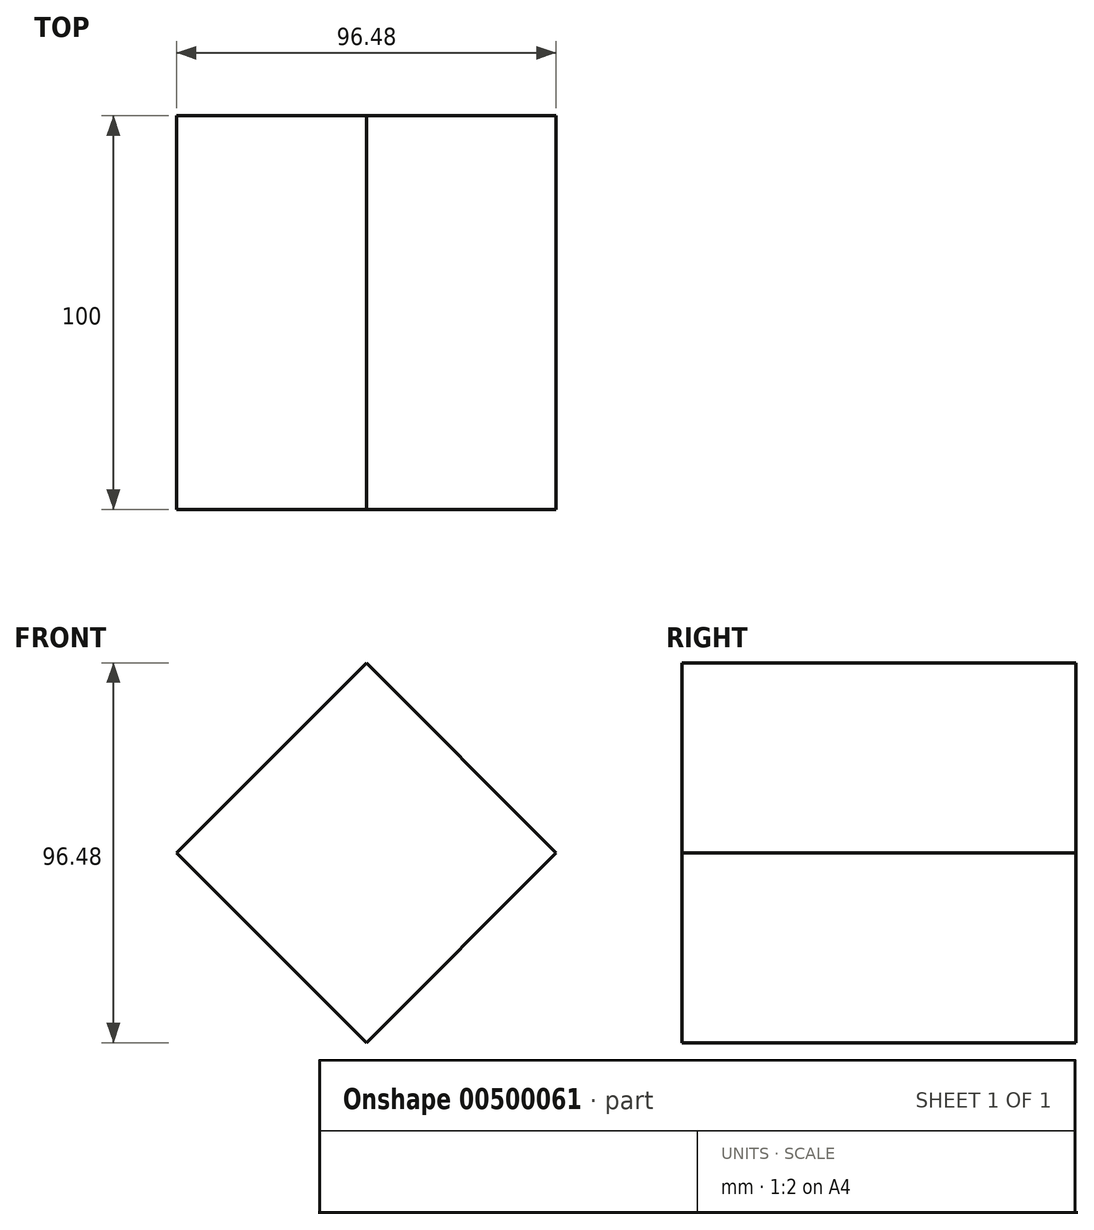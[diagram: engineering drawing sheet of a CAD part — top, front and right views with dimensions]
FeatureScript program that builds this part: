
annotation { "Feature Type Name" : "Feature", "Feature Type Description" : "" }
export const myFeature = defineFeature(function(context is Context, id is Id, definition is map)
    precondition{}
    {
        {
            var Q0;
            Q0=qCreatedBy(makeId("Front.planeOp"),FACE);
            var sketch = newSketch(context, id + "F0", { "sketchPlane" : qUnion([Q0])});
            skCircle(sketch, "E0.cCircle", {"center": v(0, 0) * mm, "radius": 48.24 * mm, "construction": true});
            skLineSegment(sketch, "E0.0", {"start": v(0, 48.24) * mm, "end": v(48.24, 0) * mm});
            skLineSegment(sketch, "E0.1", {"start": v(48.24, 0) * mm, "end": v(0, -48.24) * mm});
            skLineSegment(sketch, "E0.2", {"start": v(0, -48.24) * mm, "end": v(-48.24, 0) * mm});
            skLineSegment(sketch, "E0.3", {"start": v(-48.24, 0) * mm, "end": v(0, 48.24) * mm});
            skSolve(sketch);
        }
        {
            var Q0;
            Q0=makeQuery(id+"F0.imprint","IMPRINT",FACE,{"disambiguationData":[TD([[makeQuery(id+"F0.imprint","IMPRINT",EDGE,{"derivedFrom":sQuery(id+"F0.wireOp",EDGE,"E0.0")}),-1.0]])]});
            extrude(context, id + "F1", {"entities" : qUnion([Q0]), "depth" : 100 * mm, "symmetric" : true});
        }
    });
